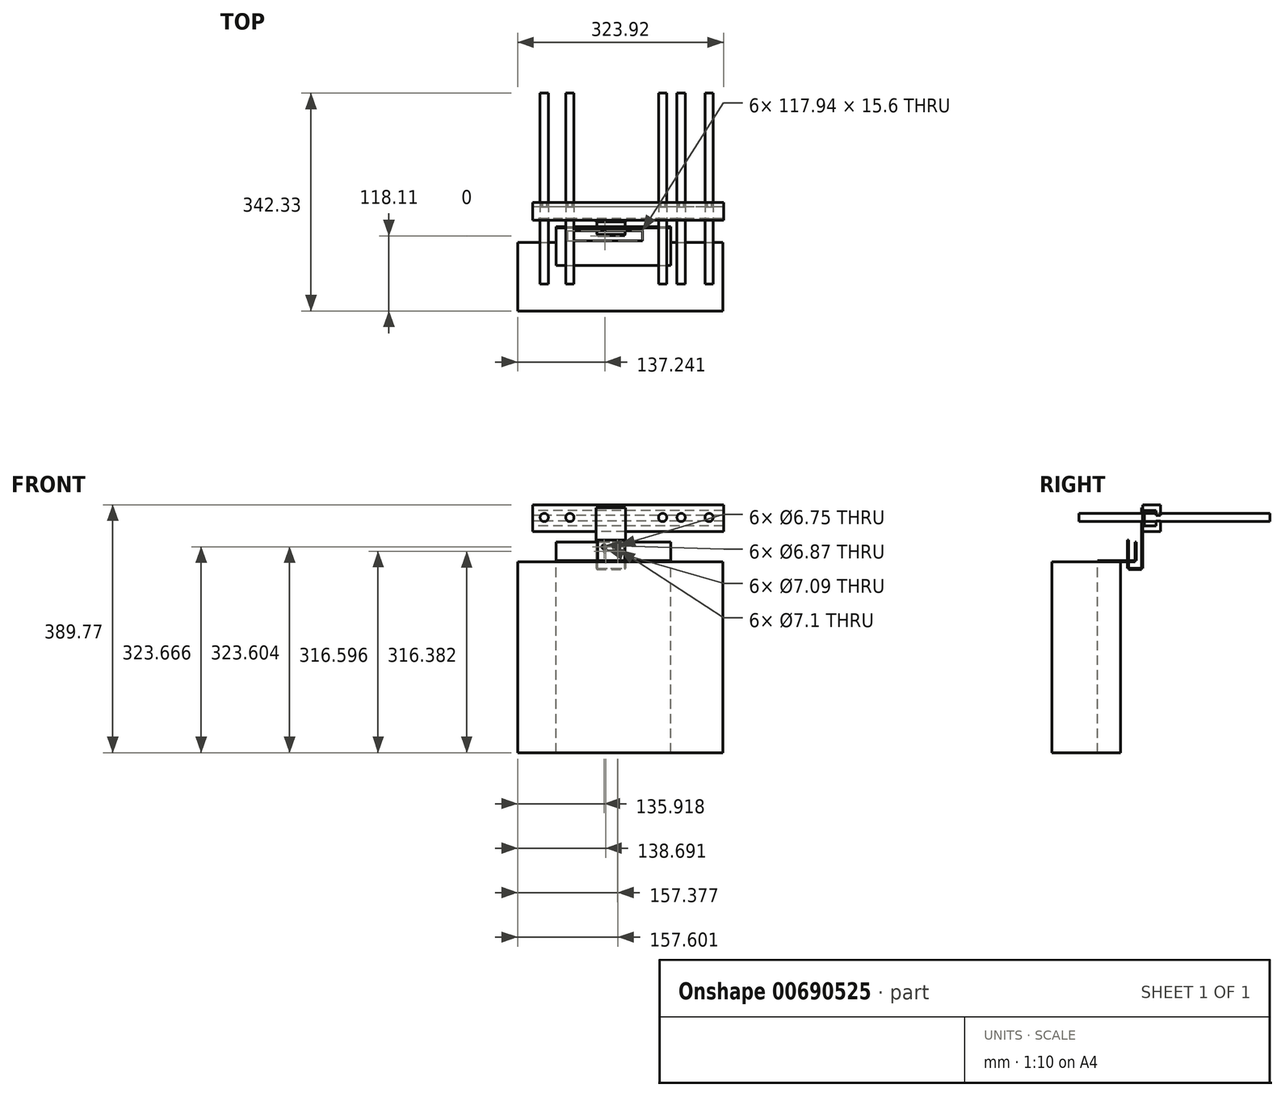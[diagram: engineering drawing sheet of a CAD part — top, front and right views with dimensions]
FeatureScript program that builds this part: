
annotation { "Feature Type Name" : "Feature", "Feature Type Description" : "" }
export const myFeature = defineFeature(function(context is Context, id is Id, definition is map)
    precondition{}
    {
        {
            var Q0;
            Q0=qCreatedBy(makeId("Right.planeOp"),FACE);
            var sketch = newSketch(context, id + "F0", { "sketchPlane" : qUnion([Q0])});
            skLineSegment(sketch, "E0", {"start": v(0, 0) * mm, "end": v(0, 42.21) * mm});
            skLineSegment(sketch, "E1", {"start": v(0, 42.21) * mm, "end": v(27.95, 42.21) * mm});
            skLineSegment(sketch, "E2", {"start": v(21.11, 33.36) * mm, "end": v(2.8, 33.36) * mm});
            skLineSegment(sketch, "E3", {"start": v(2.8, 33.36) * mm, "end": v(2.8, 8.85) * mm});
            skLineSegment(sketch, "E4", {"start": v(2.8, 8.85) * mm, "end": v(21.11, 8.85) * mm});
            skLineSegment(sketch, "E5", {"start": v(27.95, 0) * mm, "end": v(0, 0) * mm});
            skLineSegment(sketch, "E6", {"start": v(21.11, 33.36) * mm, "end": v(21.11, 25.48) * mm});
            skLineSegment(sketch, "E7", {"start": v(21.11, 25.48) * mm, "end": v(27.95, 25.48) * mm});
            skLineSegment(sketch, "E8", {"start": v(27.95, 25.48) * mm, "end": v(27.95, 42.21) * mm});
            skLineSegment(sketch, "E9", {"start": v(21.11, 8.85) * mm, "end": v(21.11, 16.73) * mm});
            skLineSegment(sketch, "E10", {"start": v(21.11, 16.73) * mm, "end": v(27.95, 16.73) * mm});
            skLineSegment(sketch, "E11", {"start": v(27.95, 16.73) * mm, "end": v(27.95, 0) * mm});
            skSolve(sketch);
        }
        {
            var Q0;
            Q0=makeQuery(id+"F0.imprint","IMPRINT",FACE,{"disambiguationData":[TD([[makeQuery(id+"F0.imprint","IMPRINT",EDGE,{"derivedFrom":sQuery(id+"F0.wireOp",EDGE,"E0")}),-1.0]])]});
            extrude(context, id + "F1", {"entities" : qUnion([Q0]), "depth" : 300 * mm, "offsetDistance" : 25 * mm});
        }
        {
            var Q0;
            Q0=makeQuery(id+"F1.opExtrude","SWEPT_FACE",FACE,{"disambiguationData":[OSD([sQuery(id+"F0.wireOp",EDGE,"E0")])]});
            var sketch = newSketch(context, id + "F2", { "sketchPlane" : qUnion([Q0])});
            skLineSegment(sketch, "E12.bottom", {"start": v(99.25, 37.99) * mm, "end": v(145.99, 37.99) * mm});
            skLineSegment(sketch, "E12.top", {"start": v(99.25, -57.56) * mm, "end": v(145.99, -57.56) * mm});
            skLineSegment(sketch, "E12.left", {"start": v(99.25, 37.99) * mm, "end": v(99.25, -57.56) * mm});
            skLineSegment(sketch, "E12.right", {"start": v(145.99, 37.99) * mm, "end": v(145.99, -57.56) * mm});
            skCircle(sketch, "E13", {"center": v(133.68, -30.96) * mm, "radius": 3.55 * mm});
            skCircle(sketch, "E14", {"center": v(114.77, -31.18) * mm, "radius": 3.55 * mm});
            skSolve(sketch);
        }
        {
            var Q0;
            {var subQ0=sQuery(id+"F2.wireOp",EDGE,"E12.bottom");Q0=makeQuery(id+"F2.imprint","IMPRINT",FACE,{"disambiguationData":[TD([[makeQuery(id+"F2.imprint","IMPRINT",EDGE,{"derivedFrom":subQ0}),-1.0]])]});}
            var Q1;
            {var subQ0=sQuery(id+"F2.wireOp",EDGE,"E12.top");Q1=makeQuery(id+"F2.imprint","IMPRINT",FACE,{"disambiguationData":[TD([[makeQuery(id+"F2.imprint","IMPRINT",EDGE,{"derivedFrom":subQ0}),1.0]])]});}
            extrude(context, id + "F3", {"entities" : qUnion([Q0, Q1]), "depth" : 2 * mm, "offsetDistance" : 25 * mm});
        }
        {
            var Q0;
            Q0=makeQuery(id+"F3.opExtrude","SWEPT_FACE",FACE,{"disambiguationData":[OSD([sQuery(id+"F2.wireOp",EDGE,"E12.top")])]});
            var sketch = newSketch(context, id + "F4", { "sketchPlane" : qUnion([Q0])});
            skLineSegment(sketch, "E15.bottom", {"start": v(100.55, 0.47) * mm, "end": v(145.23, 0.47) * mm});
            skLineSegment(sketch, "E15.top", {"start": v(100.55, 21.89) * mm, "end": v(145.23, 21.89) * mm});
            skLineSegment(sketch, "E15.left", {"start": v(100.55, 0.47) * mm, "end": v(100.55, 21.89) * mm});
            skLineSegment(sketch, "E15.right", {"start": v(145.23, 0.47) * mm, "end": v(145.23, 21.89) * mm});
            skSolve(sketch);
        }
        {
            var Q0;
            {var subQ0=sQuery(id+"F4.wireOp",EDGE,"E15.top");Q0=makeQuery(id+"F4.imprint","IMPRINT",FACE,{"disambiguationData":[TD([[makeQuery(id+"F4.imprint","IMPRINT",EDGE,{"derivedFrom":subQ0}),-1.0]])]});}
            extrude(context, id + "F5", {"entities" : qUnion([Q0]), "depth" : 2 * mm, "offsetDistance" : 25 * mm});
        }
        {
            var Q0;
            Q0=makeQuery(id+"F5.opExtrude","SWEPT_FACE",FACE,{"disambiguationData":[OSD([sQuery(id+"F4.wireOp",EDGE,"E15.top")])]});
            var sketch = newSketch(context, id + "F6", { "sketchPlane" : qUnion([Q0])});
            skLineSegment(sketch, "E16.bottom", {"start": v(144.7, -59.56) * mm, "end": v(102.1, -59.56) * mm});
            skLineSegment(sketch, "E16.top", {"start": v(144.7, -12.99) * mm, "end": v(102.1, -12.99) * mm});
            skLineSegment(sketch, "E16.left", {"start": v(144.7, -59.56) * mm, "end": v(144.7, -12.99) * mm});
            skLineSegment(sketch, "E16.right", {"start": v(102.1, -59.56) * mm, "end": v(102.1, -12.99) * mm});
            skCircle(sketch, "E17", {"center": v(133.46, -23.96) * mm, "radius": 3.37 * mm});
            skCircle(sketch, "E18", {"center": v(112, -23.9) * mm, "radius": 3.44 * mm});
            skSolve(sketch);
        }
        {
            var Q0;
            {var subQ0=sQuery(id+"F6.wireOp",EDGE,"E16.top");Q0=makeQuery(id+"F6.imprint","IMPRINT",FACE,{"disambiguationData":[TD([[makeQuery(id+"F6.imprint","IMPRINT",EDGE,{"derivedFrom":subQ0}),1.0]])]});}
            extrude(context, id + "F7", {"entities" : qUnion([Q0]), "depth" : 2 * mm, "offsetDistance" : 25 * mm});
        }
        {
            var Q0;
            Q0=makeQuery(id+"F5.opExtrude","CAP_FACE",FACE,{"disambiguationData":[OSD([sQuery(id+"F2.wireOp",EDGE,"E12.top"),sQuery(id+"F4.wireOp",EDGE,"E15.top"),sQuery(id+"F4.wireOp",EDGE,"E15.left"),sQuery(id+"F4.wireOp",EDGE,"E15.right")])],"isStart":true});
            cPlane(context, id + "F8", {"entities" : qUnion([Q0]), "cplaneType" : CPlaneType.OFFSET, "offset" : 10 * mm, "width" : 150 * mm, "height" : 150 * mm});
        }
        {
            var Q0;
            Q0=qCreatedBy(id+"F8.planeOp",FACE);
            var sketch = newSketch(context, id + "F9", { "sketchPlane" : qUnion([Q0])});
            skLineSegment(sketch, "E19.bottom", {"start": v(36.96, -71.15) * mm, "end": v(217.13, -71.15) * mm});
            skLineSegment(sketch, "E19.top", {"start": v(36.96, -11.9) * mm, "end": v(217.13, -11.9) * mm});
            skLineSegment(sketch, "E19.left", {"start": v(36.96, -71.15) * mm, "end": v(36.96, -11.9) * mm});
            skLineSegment(sketch, "E19.right", {"start": v(217.13, -71.15) * mm, "end": v(217.13, -11.9) * mm});
            skLineSegment(sketch, "E20.bottom", {"start": v(54.35, -16.42) * mm, "end": v(172.3, -16.42) * mm});
            skLineSegment(sketch, "E20.top", {"start": v(54.35, -32.02) * mm, "end": v(172.3, -32.02) * mm});
            skLineSegment(sketch, "E20.left", {"start": v(54.35, -16.42) * mm, "end": v(54.35, -32.02) * mm});
            skLineSegment(sketch, "E20.right", {"start": v(172.3, -16.42) * mm, "end": v(172.3, -32.02) * mm});
            skSolve(sketch);
        }
        {
            var Q0;
            Q0=makeQuery(id+"F9.imprint","IMPRINT",FACE,{"disambiguationData":[TD([[makeQuery(id+"F9.imprint","IMPRINT",EDGE,{"derivedFrom":sQuery(id+"F9.wireOp",EDGE,"E19.bottom")}),1.0]])]});
            extrude(context, id + "F10", {"entities" : qUnion([Q0]), "depth" : 2 * mm, "offsetDistance" : 25 * mm});
        }
        {
            var Q0;
            Q0=makeQuery(id+"F10.opExtrude","SWEPT_FACE",FACE,{"disambiguationData":[OSD([sQuery(id+"F9.wireOp",EDGE,"E19.top")])]});
            var sketch = newSketch(context, id + "F11", { "sketchPlane" : qUnion([Q0])});
            skLineSegment(sketch, "E21.bottom", {"start": v(-36.96, -45.56) * mm, "end": v(-217.13, -45.56) * mm});
            skLineSegment(sketch, "E21.top", {"start": v(-36.96, -16.09) * mm, "end": v(-217.13, -16.09) * mm});
            skLineSegment(sketch, "E21.left", {"start": v(-36.96, -45.56) * mm, "end": v(-36.96, -16.09) * mm});
            skLineSegment(sketch, "E21.right", {"start": v(-217.13, -45.56) * mm, "end": v(-217.13, -16.09) * mm});
            skCircle(sketch, "E22", {"center": v(-134.78, -30.1) * mm, "radius": 2.23 * mm});
            skCircle(sketch, "E23", {"center": v(-128.11, -25.45) * mm, "radius": 2.72 * mm});
            skSolve(sketch);
        }
        {
            var Q0;
            Q0=makeQuery(id+"F11.imprint","IMPRINT",FACE,{"disambiguationData":[TD([[makeQuery(id+"F11.imprint","IMPRINT",EDGE,{"derivedFrom":sQuery(id+"F11.wireOp",EDGE,"E21.bottom")}),-1.0]])]});
            extrude(context, id + "F12", {"entities" : qUnion([Q0]), "depth" : 2 * mm, "offsetDistance" : 25 * mm});
        }
        {
            var Q0;
            Q0=makeQuery(id+"F10.opExtrude","CAP_FACE",FACE,{"disambiguationData":[OSD([sQuery(id+"F9.wireOp",EDGE,"E19.bottom"),sQuery(id+"F9.wireOp",EDGE,"E19.top"),sQuery(id+"F9.wireOp",EDGE,"E19.left"),sQuery(id+"F9.wireOp",EDGE,"E19.right"),sQuery(id+"F9.wireOp",EDGE,"E20.bottom"),sQuery(id+"F9.wireOp",EDGE,"E20.top"),sQuery(id+"F9.wireOp",EDGE,"E20.left"),sQuery(id+"F9.wireOp",EDGE,"E20.right")])],"isStart":true});
            var sketch = newSketch(context, id + "F13", { "sketchPlane" : qUnion([Q0])});
            skLineSegment(sketch, "E24.bottom", {"start": v(-23.92, 142.33) * mm, "end": v(298.64, 142.33) * mm});
            skLineSegment(sketch, "E24.top", {"start": v(-23.92, 34.72) * mm, "end": v(298.64, 34.72) * mm});
            skLineSegment(sketch, "E24.left", {"start": v(-23.92, 142.33) * mm, "end": v(-23.92, 34.72) * mm});
            skLineSegment(sketch, "E24.right", {"start": v(298.64, 142.33) * mm, "end": v(298.64, 34.72) * mm});
            skSolve(sketch);
        }
        {
            var Q0;
            Q0=makeQuery(id+"F13.imprint","IMPRINT",FACE,{"disambiguationData":[TD([[makeQuery(id+"F13.imprint","IMPRINT",EDGE,{"derivedFrom":sQuery(id+"F13.wireOp",EDGE,"E24.bottom")}),-1.0]])]});
            extrude(context, id + "F14", {"entities" : qUnion([Q0]), "depth" : 300 * mm, "offsetDistance" : 25 * mm});
        }
        {
            var Q0;
            Q0=makeQuery(id+"F1.opExtrude","SWEPT_FACE",FACE,{"disambiguationData":[OSD([sQuery(id+"F0.wireOp",EDGE,"E0")])]});
            var sketch = newSketch(context, id + "F15", { "sketchPlane" : qUnion([Q0])});
            skCircle(sketch, "E25", {"center": v(277.27, 22.37) * mm, "radius": 6.51 * mm});
            skCircle(sketch, "E26", {"center": v(233.34, 22.37) * mm, "radius": 6.51 * mm});
            skCircle(sketch, "E27", {"center": v(18.02, 22.37) * mm, "radius": 6.51 * mm});
            skCircle(sketch, "E28", {"center": v(58.31, 22.37) * mm, "radius": 6.51 * mm});
            skCircle(sketch, "E29", {"center": v(204.28, 22.37) * mm, "radius": 6.51 * mm});
            skSolve(sketch);
        }
        {
            var Q0;
            Q0=makeQuery(id+"F15.imprint","IMPRINT",FACE,{"disambiguationData":[TD([[makeQuery(id+"F15.imprint","IMPRINT",EDGE,{"derivedFrom":sQuery(id+"F15.wireOp",EDGE,"E25")}),1.0]])]});
            var Q1;
            Q1=makeQuery(id+"F15.imprint","IMPRINT",FACE,{"disambiguationData":[TD([[makeQuery(id+"F15.imprint","IMPRINT",EDGE,{"derivedFrom":sQuery(id+"F15.wireOp",EDGE,"E26")}),1.0]])]});
            var Q2;
            Q2=makeQuery(id+"F15.imprint","IMPRINT",FACE,{"disambiguationData":[TD([[makeQuery(id+"F15.imprint","IMPRINT",EDGE,{"derivedFrom":sQuery(id+"F15.wireOp",EDGE,"E29")}),1.0]])]});
            var Q3;
            Q3=makeQuery(id+"F15.imprint","IMPRINT",FACE,{"disambiguationData":[TD([[makeQuery(id+"F15.imprint","IMPRINT",EDGE,{"derivedFrom":sQuery(id+"F15.wireOp",EDGE,"E28")}),1.0]])]});
            var Q4;
            Q4=makeQuery(id+"F15.imprint","IMPRINT",FACE,{"disambiguationData":[TD([[makeQuery(id+"F15.imprint","IMPRINT",EDGE,{"derivedFrom":sQuery(id+"F15.wireOp",EDGE,"E27")}),1.0]])]});
            extrude(context, id + "F16", {"entities" : qUnion([Q0, Q1, Q2, Q3, Q4]), "operationType" : NewBodyOperationType.ADD, "depth" : 100 * mm, "offsetDistance" : 25 * mm});
        }
        {
            var Q0;
            Q0=makeQuery(id+"F15.imprint","IMPRINT",FACE,{"disambiguationData":[TD([[makeQuery(id+"F15.imprint","IMPRINT",EDGE,{"derivedFrom":sQuery(id+"F15.wireOp",EDGE,"E25")}),1.0]])]});
            var Q1;
            Q1=makeQuery(id+"F15.imprint","IMPRINT",FACE,{"disambiguationData":[TD([[makeQuery(id+"F15.imprint","IMPRINT",EDGE,{"derivedFrom":sQuery(id+"F15.wireOp",EDGE,"E26")}),1.0]])]});
            var Q2;
            Q2=makeQuery(id+"F15.imprint","IMPRINT",FACE,{"disambiguationData":[TD([[makeQuery(id+"F15.imprint","IMPRINT",EDGE,{"derivedFrom":sQuery(id+"F15.wireOp",EDGE,"E29")}),1.0]])]});
            var Q3;
            Q3=makeQuery(id+"F15.imprint","IMPRINT",FACE,{"disambiguationData":[TD([[makeQuery(id+"F15.imprint","IMPRINT",EDGE,{"derivedFrom":sQuery(id+"F15.wireOp",EDGE,"E28")}),1.0]])]});
            var Q4;
            Q4=makeQuery(id+"F15.imprint","IMPRINT",FACE,{"disambiguationData":[TD([[makeQuery(id+"F15.imprint","IMPRINT",EDGE,{"derivedFrom":sQuery(id+"F15.wireOp",EDGE,"E27")}),1.0]])]});
            extrude(context, id + "F17", {"entities" : qUnion([Q0, Q1, Q2, Q3, Q4]), "oppositeDirection" : true, "depth" : 200 * mm, "offsetDistance" : 25 * mm});
        }
    });
